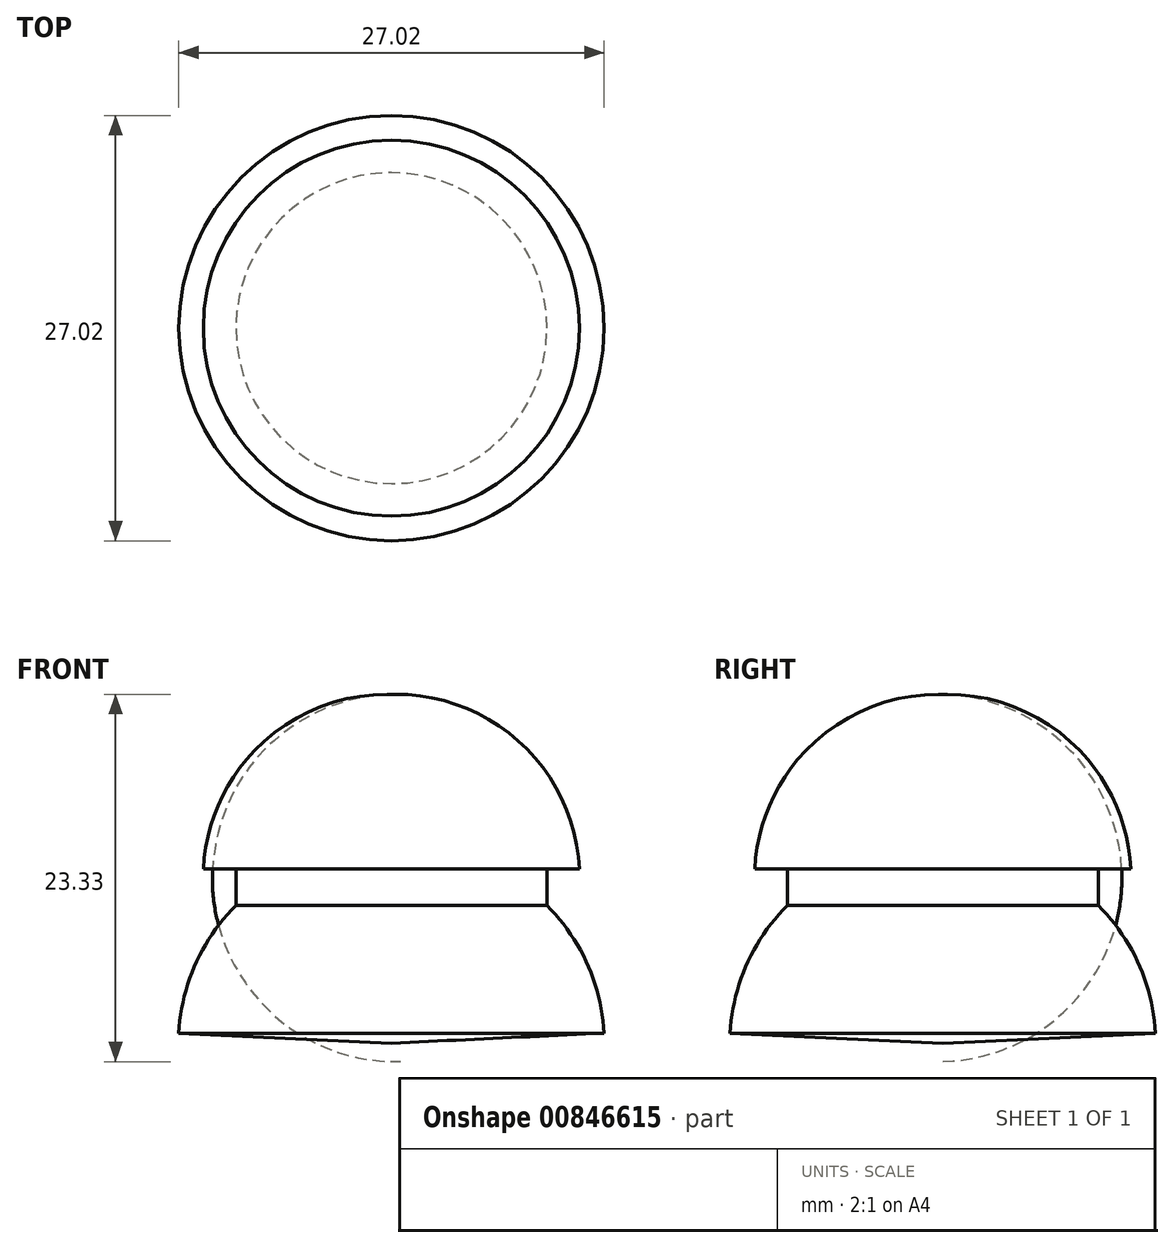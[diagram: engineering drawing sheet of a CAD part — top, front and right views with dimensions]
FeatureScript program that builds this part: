
annotation { "Feature Type Name" : "Feature", "Feature Type Description" : "" }
export const myFeature = defineFeature(function(context is Context, id is Id, definition is map)
    precondition{}
    {
        {
            var Q0;
            Q0=qCreatedBy(makeId("Front.planeOp"),FACE);
            var sketch = newSketch(context, id + "F0", { "sketchPlane" : qUnion([Q0])});
            skArc(sketch, "E0", {"start": v(0, 11.08) * mm, "mid": v(-8.23, 7.97) * mm, "end": v(-11.94, 0) * mm});
            skLineSegment(sketch, "E1", {"start": v(-11.94, 0) * mm, "end": v(0, 0) * mm});
            skLineSegment(sketch, "E2", {"start": v(-9.88, 0) * mm, "end": v(-9.88, -2.33) * mm});
            skLineSegment(sketch, "E3", {"start": v(-9.88, -2.33) * mm, "end": v(0, -2.33) * mm});
            skLineSegment(sketch, "E4", {"start": v(0, -2.33) * mm, "end": v(-0.3, -0.58) * mm});
            skArc(sketch, "E5", {"start": v(-9.88, -2.33) * mm, "mid": v(-12.45, -6.05) * mm, "end": v(-13.5, -10.44) * mm});
            skLineSegment(sketch, "E6", {"start": v(-13.5, -10.44) * mm, "end": v(0, -11.08) * mm});
            skLineSegment(sketch, "E7", {"start": v(0, -11.08) * mm, "end": v(0, -2.33) * mm});
            skLineSegment(sketch, "E8", {"start": v(0, 11.08) * mm, "end": v(0, -2.33) * mm});
            skSolve(sketch);
        }
        {
            var Q0;
            {var subQ0=sQuery(id+"F0.wireOp",EDGE,"E0");Q0=makeQuery(id+"F0.imprint","IMPRINT",FACE,{"disambiguationData":[TD([[makeQuery(id+"F0.imprint","IMPRINT",EDGE,{"derivedFrom":subQ0}),1.0]])]});}
            var Q1;
            {var subQ3=sQuery(id+"F0.wireOp",EDGE,"E2");Q1=makeQuery(id+"F0.imprint","IMPRINT",FACE,{"disambiguationData":[TD([[makeQuery(id+"F0.imprint","IMPRINT",EDGE,{"derivedFrom":subQ3}),1.0]])]});}
            var Q2;
            Q2=makeQuery(id+"F0.imprint","IMPRINT",FACE,{"disambiguationData":[TD([[makeQuery(id+"F0.imprint","IMPRINT",EDGE,{"derivedFrom":sQuery(id+"F0.wireOp",EDGE,"E3")}),-1.0]])]});
            var Q3;
            Q3=sQuery(id+"F0.wireOp",EDGE,"E8");
            revolve(context, id + "F1", {"surfaceOperationType" : NewSurfaceOperationType.NEW, "entities" : qUnion([Q0, Q1, Q2]), "axis" : qUnion([Q3]), "revolveType" : RevolveType.FULL});
        }
    });
